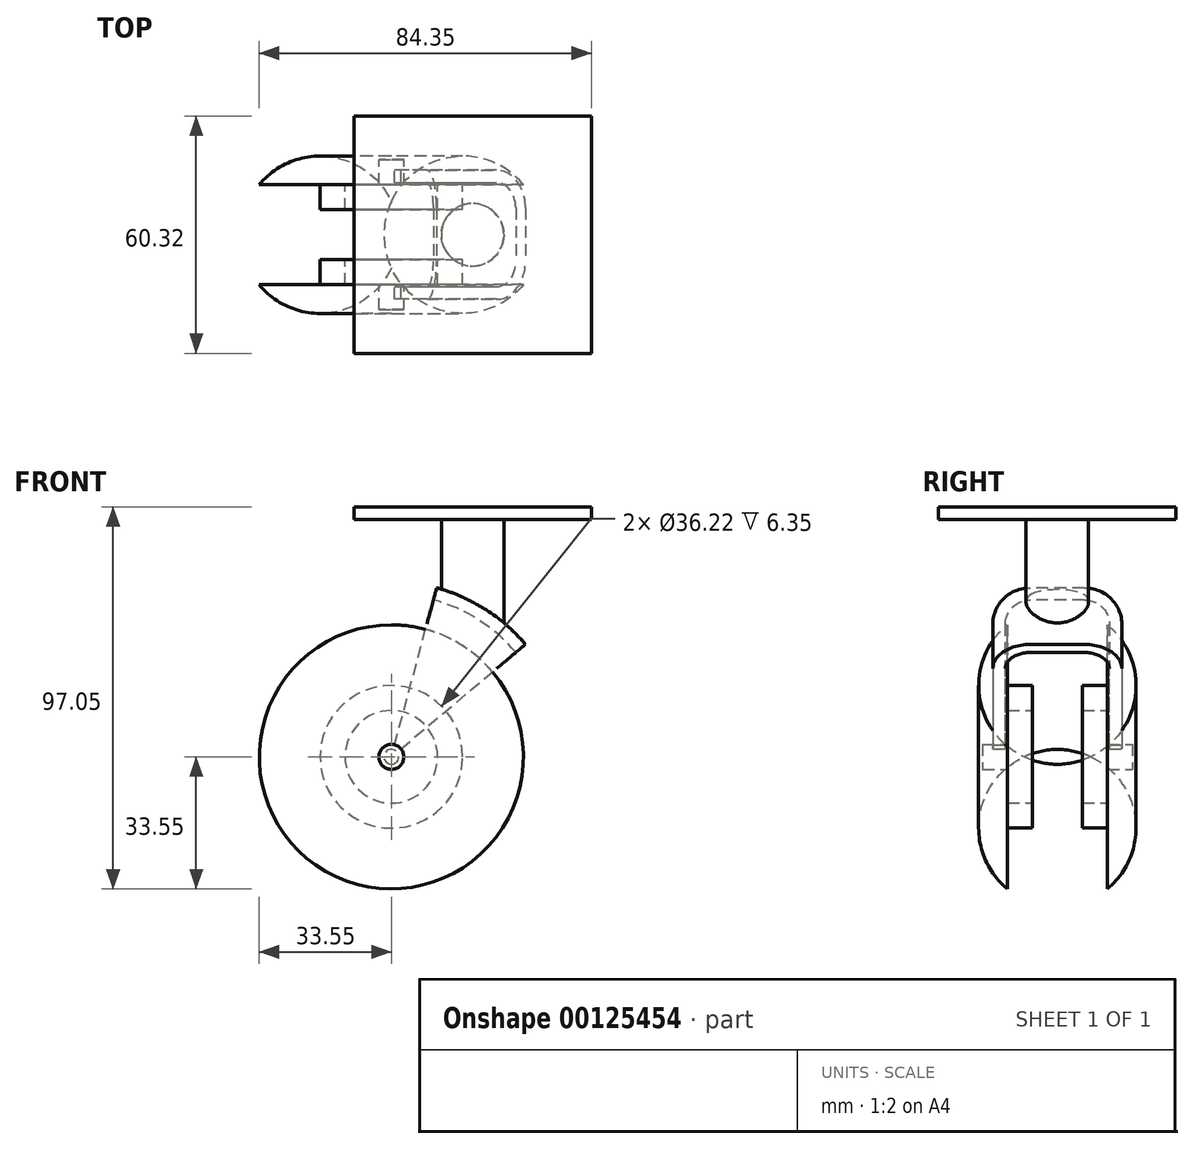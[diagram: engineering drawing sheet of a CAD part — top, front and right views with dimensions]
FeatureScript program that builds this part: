
annotation { "Feature Type Name" : "Feature", "Feature Type Description" : "" }
export const myFeature = defineFeature(function(context is Context, id is Id, definition is map)
    precondition{}
    {
        {
            var Q0;
            Q0=qCreatedBy(makeId("Top.planeOp"),FACE);
            var sketch = newSketch(context, id + "F0", { "sketchPlane" : qUnion([Q0])});
            skLineSegment(sketch, "E0", {"start": v(0, 42.19) * mm, "end": v(0, -42.19) * mm, "construction": true});
            skLineSegment(sketch, "E1", {"start": v(0, 0) * mm, "end": v(19.05, 0) * mm, "construction": true});
            skLineSegment(sketch, "E2", {"start": v(3.17, -12.7) * mm, "end": v(11.76, -12.7) * mm});
            skLineSegment(sketch, "E3", {"start": v(11.76, -12.7) * mm, "end": v(11.76, -6.35) * mm});
            skLineSegment(sketch, "E4", {"start": v(11.76, -6.35) * mm, "end": v(18.11, -6.35) * mm});
            skLineSegment(sketch, "E5", {"start": v(18.11, -6.35) * mm, "end": v(18.11, -12.7) * mm});
            skLineSegment(sketch, "E6", {"start": v(18.11, -12.7) * mm, "end": v(33.55, -12.7) * mm});
            skLineSegment(sketch, "E7.MirrorCS", {"start": v(11.76, 12.7) * mm, "end": v(11.76, 6.35) * mm});
            skLineSegment(sketch, "E8.MirrorCS", {"start": v(11.76, 6.35) * mm, "end": v(18.11, 6.35) * mm});
            skLineSegment(sketch, "E9.MirrorCS", {"start": v(18.11, 6.35) * mm, "end": v(18.11, 12.7) * mm});
            skLineSegment(sketch, "E10.MirrorCS", {"start": v(18.11, 12.7) * mm, "end": v(33.55, 12.7) * mm});
            skLineSegment(sketch, "E11.MirrorCS", {"start": v(3.17, 12.7) * mm, "end": v(11.76, 12.7) * mm});
            skArc(sketch, "E12", {"start": v(33.55, -12.7) * mm, "mid": v(38.1, 0) * mm, "end": v(33.55, 12.7) * mm});
            skLineSegment(sketch, "E13", {"start": v(0, 19.05) * mm, "end": v(0, -19.05) * mm});
            skLineSegment(sketch, "E14", {"start": v(3.17, 12.7) * mm, "end": v(3.17, 19.05) * mm});
            skLineSegment(sketch, "E15", {"start": v(3.17, 19.05) * mm, "end": v(0, 19.05) * mm});
            skLineSegment(sketch, "E16.MirrorCS", {"start": v(3.17, -19.05) * mm, "end": v(0, -19.05) * mm});
            skLineSegment(sketch, "E17.MirrorCS", {"start": v(3.17, -12.7) * mm, "end": v(3.17, -19.05) * mm});
            skSolve(sketch);
        }
        {
            var Q0;
            Q0=makeQuery(id+"F0.imprint","IMPRINT",FACE,{"disambiguationData":[TD([[makeQuery(id+"F0.imprint","IMPRINT",EDGE,{"derivedFrom":sQuery(id+"F0.wireOp",EDGE,"E2")}),1.0]])]});
            var Q1;
            Q1=sQuery(id+"F0.wireOp",EDGE,"E0");
            revolve(context, id + "F1", {"entities" : qUnion([Q0]), "axis" : qUnion([Q1]), "revolveType" : RevolveType.FULL});
        }
        {
            var Q0;
            Q0=qCreatedBy(makeId("Top.planeOp"),FACE);
            var sketch = newSketch(context, id + "F2", { "sketchPlane" : qUnion([Q0])});
            skLineSegment(sketch, "E18", {"start": v(0, 0) * mm, "end": v(60.2, 0) * mm, "construction": true});
            skLineSegment(sketch, "E19", {"start": v(0, 0) * mm, "end": v(0, 46.98) * mm, "construction": true});
            skLineSegment(sketch, "E20", {"start": v(0, 13.2) * mm, "end": v(34.93, 13.2) * mm});
            skLineSegment(sketch, "E21", {"start": v(41.28, 6.86) * mm, "end": v(41.28, 0) * mm});
            skLineSegment(sketch, "E22", {"start": v(44.45, 0) * mm, "end": v(44.45, 6.86) * mm});
            skLineSegment(sketch, "E23", {"start": v(34.93, 16.38) * mm, "end": v(0, 16.38) * mm});
            skLineSegment(sketch, "E24", {"start": v(0, 16.38) * mm, "end": v(0, 13.2) * mm});
            skPoint(sketch, "E25.visualSharp", {"position": v(41.28, 13.2) * mm});
            skArc(sketch, "E25.filletArc", {"start": v(41.28, 6.86) * mm, "mid": v(39.42, 11.35) * mm, "end": v(34.93, 13.2) * mm});
            skPoint(sketch, "E26.visualSharp", {"position": v(44.45, 16.38) * mm});
            skArc(sketch, "E26.filletArc", {"start": v(44.45, 6.86) * mm, "mid": v(41.66, 13.6) * mm, "end": v(34.93, 16.38) * mm});
            skLineSegment(sketch, "E27.MirrorCS", {"start": v(44.45, 0) * mm, "end": v(44.45, -6.86) * mm});
            skLineSegment(sketch, "E28.MirrorCS", {"start": v(41.28, -6.86) * mm, "end": v(41.28, 0) * mm});
            skArc(sketch, "E29.MirrorCS", {"start": v(44.45, -6.86) * mm, "mid": v(41.66, -13.6) * mm, "end": v(34.93, -16.38) * mm});
            skArc(sketch, "E30.MirrorCS", {"start": v(41.28, -6.86) * mm, "mid": v(39.42, -11.35) * mm, "end": v(34.93, -13.2) * mm});
            skLineSegment(sketch, "E31.MirrorCS", {"start": v(34.93, -16.38) * mm, "end": v(0, -16.38) * mm});
            skLineSegment(sketch, "E32.MirrorCS", {"start": v(0, -13.2) * mm, "end": v(34.93, -13.2) * mm});
            skLineSegment(sketch, "E33.MirrorCS", {"start": v(0, -16.38) * mm, "end": v(0, -13.2) * mm});
            skSolve(sketch);
        }
        {
            var Q0;
            Q0=makeQuery(id+"F2.imprint","IMPRINT",FACE,{"disambiguationData":[TD([[makeQuery(id+"F2.imprint","IMPRINT",EDGE,{"derivedFrom":sQuery(id+"F2.wireOp",EDGE,"E20")}),1.0]])]});
            var Q1;
            Q1=sQuery(id+"F2.wireOp",EDGE,"E19");
            revolve(context, id + "F3", {"operationType" : NewBodyOperationType.ADD, "entities" : qUnion([Q0]), "axis" : qUnion([Q1]), "revolveType" : RevolveType.TWO_DIRECTIONS, "oppositeDirection" : true, "angle" : 75 * degree, "angleBack" : 40 * degree});
        }
        {
            var Q0;
            Q0=qCreatedBy(makeId("Top.planeOp"),FACE);
            cPlane(context, id + "F4", {"entities" : qUnion([Q0]), "cplaneType" : CPlaneType.OFFSET, "offset" : 63.5 * mm, "width" : 152.4 * mm, "height" : 152.4 * mm});
        }
        {
            var Q0;
            Q0=qCreatedBy(id+"F4.planeOp",FACE);
            var sketch = newSketch(context, id + "F5", { "sketchPlane" : qUnion([Q0])});
            skLineSegment(sketch, "E34.bottom", {"start": v(-9.52, 30.16) * mm, "end": v(50.8, 30.16) * mm});
            skLineSegment(sketch, "E34.top", {"start": v(-9.52, -30.16) * mm, "end": v(50.8, -30.16) * mm});
            skLineSegment(sketch, "E34.left", {"start": v(-9.52, 30.16) * mm, "end": v(-9.53, -30.16) * mm});
            skLineSegment(sketch, "E34.right", {"start": v(50.8, 30.16) * mm, "end": v(50.8, -30.16) * mm});
            skLineSegment(sketch, "E35", {"start": v(-9.52, 0) * mm, "end": v(0, 0) * mm, "construction": true});
            skSolve(sketch);
        }
        {
            var Q0;
            Q0=qCreatedBy(id+"F4.planeOp",FACE);
            var sketch = newSketch(context, id + "F6", { "sketchPlane" : qUnion([Q0])});
            skCircle(sketch, "E36", {"center": v(20.64, 0) * mm, "radius": 7.94 * mm});
            skLineSegment(sketch, "E37", {"start": v(20.64, 0) * mm, "end": v(-9.52, 0) * mm, "construction": true});
            skLineSegment(sketch, "E38", {"start": v(20.64, 0) * mm, "end": v(20.64, 30.16) * mm, "construction": true});
            skSolve(sketch);
        }
        {
            var Q0;
            Q0 = qSketchRegion(id + "F6", true);
            extrude(context, id + "F7", {"entities" : qUnion([Q0]), "operationType" : NewBodyOperationType.ADD, "endBound" : BoundingType.UP_TO_NEXT, "oppositeDirection" : true, "depth" : 25.4 * mm});
        }
        {
            var Q0;
            Q0 = qSketchRegion(id + "F5", true);
            extrude(context, id + "F8", {"entities" : qUnion([Q0]), "operationType" : NewBodyOperationType.ADD, "oppositeDirection" : true, "depth" : 3.17 * mm});
        }
    });
